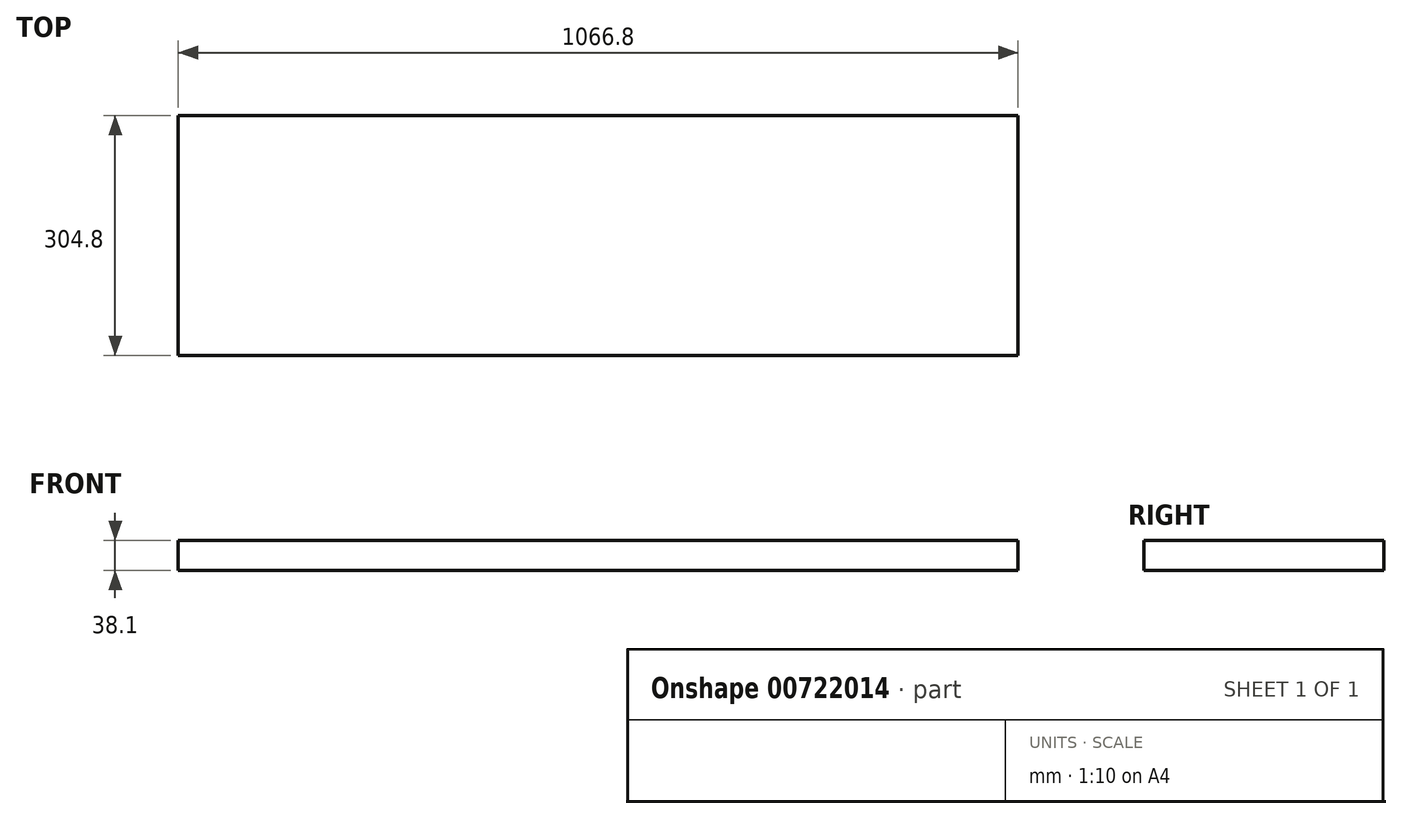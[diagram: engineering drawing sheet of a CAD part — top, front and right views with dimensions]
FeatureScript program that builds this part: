
annotation { "Feature Type Name" : "Feature", "Feature Type Description" : "" }
export const myFeature = defineFeature(function(context is Context, id is Id, definition is map)
    precondition{}
    {
        {
            var Q0;
            Q0=qCreatedBy(makeId("Top.planeOp"),FACE);
            var sketch = newSketch(context, id + "F0", { "sketchPlane" : qUnion([Q0])});
            skLineSegment(sketch, "E0.bottom", {"start": v(-317.55, -239.14) * mm, "end": v(749.25, -239.14) * mm});
            skLineSegment(sketch, "E0.top", {"start": v(-317.55, -543.94) * mm, "end": v(749.25, -543.94) * mm});
            skLineSegment(sketch, "E0.left", {"start": v(-317.55, -239.14) * mm, "end": v(-317.55, -543.94) * mm});
            skLineSegment(sketch, "E0.right", {"start": v(749.25, -239.14) * mm, "end": v(749.25, -543.94) * mm});
            skSolve(sketch);
        }
        {
            var Q0;
            Q0 = qSketchRegion(id + "F0", true);
            extrude(context, id + "F1", {"entities" : qUnion([Q0]), "depth" : 38.1 * mm, "offsetDistance" : 25.4 * mm});
        }
    });
